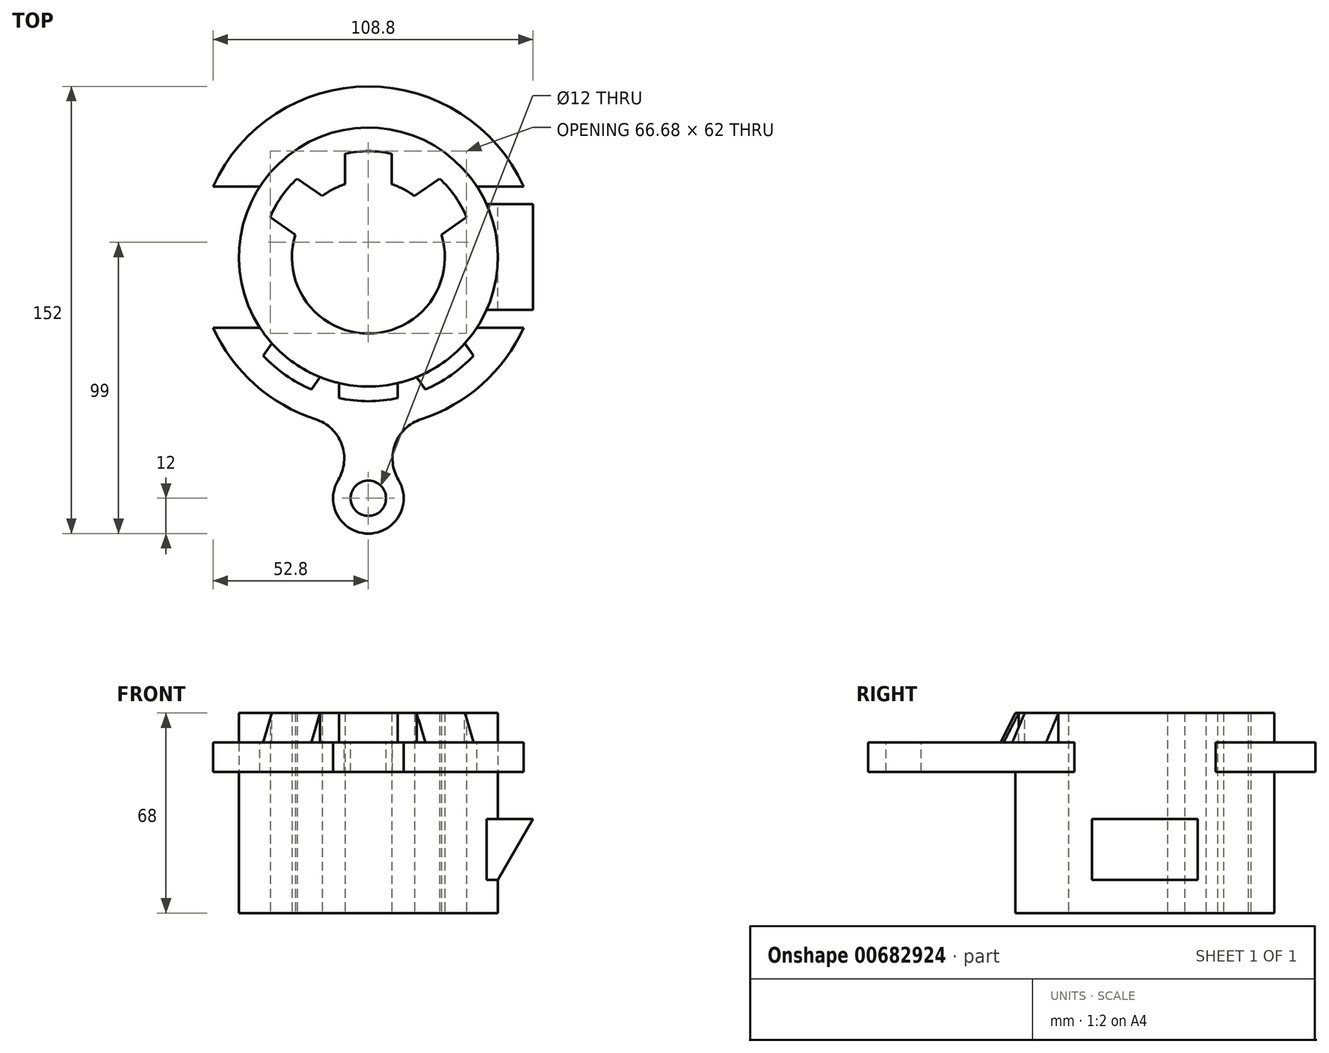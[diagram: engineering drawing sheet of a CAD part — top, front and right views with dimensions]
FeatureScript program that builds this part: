
annotation { "Feature Type Name" : "Feature", "Feature Type Description" : "" }
export const myFeature = defineFeature(function(context is Context, id is Id, definition is map)
    precondition{}
    {
        {
            var Q0;
            Q0=qCreatedBy(makeId("Top.planeOp"),FACE);
            var sketch = newSketch(context, id + "F0", { "sketchPlane" : qUnion([Q0])});
            skCircle(sketch, "E0", {"center": v(0, 0) * mm, "radius": 44 * mm});
            skArc(sketch, "E1", {"start": v(-8, 24.74) * mm, "mid": v(-12, -23.06) * mm, "end": v(24.85, 7.64) * mm});
            skLineSegment(sketch, "E2", {"start": v(-8, 24.74) * mm, "end": v(-8, 35.1) * mm});
            skLineSegment(sketch, "E3", {"start": v(8, 24.74) * mm, "end": v(8, 35.1) * mm});
            skArc(sketch, "E4", {"start": v(8, 35.1) * mm, "mid": v(0, 36) * mm, "end": v(-8, 35.1) * mm});
            skLineSegment(sketch, "E5", {"start": v(15.68, 20.74) * mm, "end": v(24.16, 26.69) * mm});
            skLineSegment(sketch, "E6", {"start": v(24.85, 7.64) * mm, "end": v(33.34, 13.58) * mm});
            skArc(sketch, "E7", {"start": v(33.34, 13.58) * mm, "mid": v(29.49, 20.65) * mm, "end": v(24.16, 26.69) * mm});
            skArc(sketch, "E8.trimOffspring", {"start": v(15.68, 20.74) * mm, "mid": v(12, 23.06) * mm, "end": v(8, 24.74) * mm});
            skLineSegment(sketch, "E9.1.0", {"start": v(-24.85, 7.64) * mm, "end": v(-33.34, 13.58) * mm});
            skArc(sketch, "E9.1.1", {"start": v(-24.16, 26.69) * mm, "mid": v(-29.49, 20.65) * mm, "end": v(-33.34, 13.58) * mm});
            skLineSegment(sketch, "E9.1.2", {"start": v(-15.68, 20.74) * mm, "end": v(-24.16, 26.69) * mm});
            skLineSegment(sketch, "E9.anchor1", {"start": v(0, 0) * mm, "end": v(15.68, 20.74) * mm, "construction": true});
            skLineSegment(sketch, "E9.anchor2", {"start": v(0, 0) * mm, "end": v(-24.85, 7.64) * mm, "construction": true});
            skSolve(sketch);
        }
        {
            var Q0;
            Q0=makeQuery(id+"F0.imprint","IMPRINT",FACE,{"disambiguationData":[TD([[makeQuery(id+"F0.imprint","IMPRINT",EDGE,{"derivedFrom":sQuery(id+"F0.wireOp",EDGE,"E0")}),1.0]])]});
            extrude(context, id + "F1", {"entities" : qUnion([Q0]), "endBound" : BoundingType.SYMMETRIC, "depth" : 68 * mm, "offsetDistance" : 25 * mm});
        }
        {
            var Q0;
            Q0=makeQuery(id+"F1.opExtrude","CAP_FACE",FACE,{"disambiguationData":[OSD([sQuery(id+"F0.wireOp",EDGE,"E0"),sQuery(id+"F0.wireOp",EDGE,"E1"),sQuery(id+"F0.wireOp",EDGE,"E2"),sQuery(id+"F0.wireOp",EDGE,"E3"),sQuery(id+"F0.wireOp",EDGE,"E4"),sQuery(id+"F0.wireOp",EDGE,"E5"),sQuery(id+"F0.wireOp",EDGE,"E6"),sQuery(id+"F0.wireOp",EDGE,"E7"),sQuery(id+"F0.wireOp",EDGE,"E8.trimOffspring"),sQuery(id+"F0.wireOp",EDGE,"E9.1.0"),sQuery(id+"F0.wireOp",EDGE,"E9.1.1"),sQuery(id+"F0.wireOp",EDGE,"E9.1.2")])],"isStart":false});
            cPlane(context, id + "F2", {"entities" : qUnion([Q0]), "cplaneType" : CPlaneType.OFFSET, "offset" : 10 * mm, "oppositeDirection" : true, "width" : 150 * mm, "height" : 150 * mm});
        }
        {
            var Q0;
            Q0=qCreatedBy(id+"F2.planeOp",FACE);
            var sketch = newSketch(context, id + "F3", { "sketchPlane" : qUnion([Q0])});
            skArc(sketch, "E10", {"start": v(-52.8, -24) * mm, "mid": v(-38.63, -43.26) * mm, "end": v(-17.9, -55.17) * mm});
            skLineSegment(sketch, "E11", {"start": v(-52.8, -24) * mm, "end": v(52.8, -24) * mm});
            skLineSegment(sketch, "E12", {"start": v(-52.8, 24) * mm, "end": v(52.8, 24) * mm});
            skArc(sketch, "E13.trimOffspring", {"start": v(52.8, 24) * mm, "mid": v(0, 58) * mm, "end": v(-52.8, 24) * mm});
            skCircle(sketch, "E14.0", {"center": v(0, 0) * mm, "radius": 44 * mm});
            skArc(sketch, "E15", {"start": v(-10.25, -75.76) * mm, "mid": v(0, -94) * mm, "end": v(10.25, -75.76) * mm});
            skCircle(sketch, "E16", {"center": v(0, -82) * mm, "radius": 6 * mm});
            skArc(sketch, "E17", {"start": v(-10.25, -75.76) * mm, "mid": v(-9.09, -63.62) * mm, "end": v(-17.9, -55.17) * mm});
            skArc(sketch, "E18", {"start": v(17.9, -55.17) * mm, "mid": v(9.09, -63.62) * mm, "end": v(10.25, -75.76) * mm});
            skArc(sketch, "E19.trimOffspring", {"start": v(17.9, -55.17) * mm, "mid": v(38.63, -43.26) * mm, "end": v(52.8, -24) * mm});
            skSolve(sketch);
        }
        {
            var Q0;
            {var subQ4=sQuery(id+"F3.wireOp",EDGE,"E10");Q0=makeQuery(id+"F3.imprint","IMPRINT",FACE,{"disambiguationData":[TD([[makeQuery(id+"F3.imprint","IMPRINT",EDGE,{"derivedFrom":subQ4}),1.0]])]});}
            var Q1;
            {var subQ0=sQuery(id+"F3.wireOp",EDGE,"E13.trimOffspring");Q1=makeQuery(id+"F3.imprint","IMPRINT",FACE,{"disambiguationData":[TD([[makeQuery(id+"F3.imprint","IMPRINT",EDGE,{"derivedFrom":subQ0}),1.0]])]});}
            extrude(context, id + "F4", {"entities" : qUnion([Q0, Q1]), "operationType" : NewBodyOperationType.ADD, "oppositeDirection" : true, "depth" : 10 * mm, "offsetDistance" : 25 * mm});
        }
        {
            var Q0;
            Q0=qCreatedBy(makeId("Front.planeOp"),FACE);
            var sketch = newSketch(context, id + "F5", { "sketchPlane" : qUnion([Q0])});
            skLineSegment(sketch, "E20", {"start": v(44, 34) * mm, "end": v(44, -34) * mm});
            skLineSegment(sketch, "E21", {"start": v(44, -2) * mm, "end": v(56, -2) * mm});
            skLineSegment(sketch, "E22", {"start": v(56, -2) * mm, "end": v(44, -22.78) * mm});
            skLineSegment(sketch, "E23", {"start": v(44, -22.78) * mm, "end": v(31.63, -22.78) * mm});
            skLineSegment(sketch, "E24", {"start": v(31.63, -22.78) * mm, "end": v(31.63, -2) * mm});
            skLineSegment(sketch, "E25", {"start": v(31.63, -2) * mm, "end": v(44, -2) * mm});
            skLineSegment(sketch, "E26.0", {"start": v(-44, -34) * mm, "end": v(44, -34) * mm});
            skSolve(sketch);
        }
        {
            var Q0;
            Q0 = qSketchRegion(id + "F5", true);
            extrude(context, id + "F6", {"entities" : qUnion([Q0]), "operationType" : NewBodyOperationType.ADD, "endBound" : BoundingType.SYMMETRIC, "depth" : 36 * mm, "offsetDistance" : 25 * mm});
        }
        {
            var Q0;
            Q0=makeQuery(id+"F1.opExtrude","CAP_FACE",FACE,{"disambiguationData":[OSD([sQuery(id+"F0.wireOp",EDGE,"E0"),sQuery(id+"F0.wireOp",EDGE,"E1"),sQuery(id+"F0.wireOp",EDGE,"E2"),sQuery(id+"F0.wireOp",EDGE,"E3"),sQuery(id+"F0.wireOp",EDGE,"E4"),sQuery(id+"F0.wireOp",EDGE,"E5"),sQuery(id+"F0.wireOp",EDGE,"E6"),sQuery(id+"F0.wireOp",EDGE,"E7"),sQuery(id+"F0.wireOp",EDGE,"E8.trimOffspring"),sQuery(id+"F0.wireOp",EDGE,"E9.1.0"),sQuery(id+"F0.wireOp",EDGE,"E9.1.1"),sQuery(id+"F0.wireOp",EDGE,"E9.1.2")])],"isStart":false});
            var sketch = newSketch(context, id + "F7", { "sketchPlane" : qUnion([Q0])});
            skCircle(sketch, "E27.0", {"center": v(0, 0) * mm, "radius": 44 * mm});
            skLineSegment(sketch, "E28", {"start": v(-10, -42.85) * mm, "end": v(-10, -47.97) * mm});
            skCircle(sketch, "E29", {"center": v(0, 0) * mm, "radius": 49 * mm});
            skLineSegment(sketch, "E30", {"start": v(10, -42.85) * mm, "end": v(10, -47.97) * mm});
            skLineSegment(sketch, "E31", {"start": v(0, 0) * mm, "end": v(0, -60.57) * mm, "construction": true});
            skLineSegment(sketch, "E32", {"start": v(16.39, -40.84) * mm, "end": v(32.77, -29.36) * mm});
            skLineSegment(sketch, "E33", {"start": v(0, 0) * mm, "end": v(25.24, -36.04) * mm});
            skLineSegment(sketch, "E34", {"start": v(16.39, -40.84) * mm, "end": v(19.32, -45.03) * mm});
            skLineSegment(sketch, "E35", {"start": v(32.77, -29.36) * mm, "end": v(35.7, -33.56) * mm});
            skLineSegment(sketch, "E36", {"start": v(-16.39, -40.84) * mm, "end": v(-19.32, -45.03) * mm});
            skLineSegment(sketch, "E37", {"start": v(-32.77, -29.36) * mm, "end": v(-35.7, -33.56) * mm});
            skLineSegment(sketch, "E38", {"start": v(-32.77, -29.36) * mm, "end": v(-16.39, -40.84) * mm});
            skLineSegment(sketch, "E39", {"start": v(0, 0) * mm, "end": v(-24.58, -35.1) * mm});
            skSolve(sketch);
        }
        {
            var Q0;
            {var subQ1=sQuery(id+"F7.wireOp",EDGE,"E36");Q0=makeQuery(id+"F7.imprint","IMPRINT",FACE,{"disambiguationData":[TD([[makeQuery(id+"F7.imprint","IMPRINT",EDGE,{"derivedFrom":subQ1}),-1.0]])]});}
            var Q1;
            {var subQ0=sQuery(id+"F7.wireOp",EDGE,"E28");Q1=makeQuery(id+"F7.imprint","IMPRINT",FACE,{"disambiguationData":[TD([[makeQuery(id+"F7.imprint","IMPRINT",EDGE,{"derivedFrom":subQ0}),1.0]])]});}
            var Q2;
            {var subQ0=sQuery(id+"F7.wireOp",EDGE,"E34");Q2=makeQuery(id+"F7.imprint","IMPRINT",FACE,{"disambiguationData":[TD([[makeQuery(id+"F7.imprint","IMPRINT",EDGE,{"derivedFrom":subQ0}),1.0]])]});}
            var Q3;
            Q3=makeQuery(id+"F4.opExtrude","CAP_FACE",FACE,{"disambiguationData":[OSD([sQuery(id+"F3.wireOp",EDGE,"E10"),sQuery(id+"F3.wireOp",EDGE,"E11"),sQuery(id+"F3.wireOp",EDGE,"E14.0"),sQuery(id+"F3.wireOp",EDGE,"E15"),sQuery(id+"F3.wireOp",EDGE,"E16"),sQuery(id+"F3.wireOp",EDGE,"E17"),sQuery(id+"F3.wireOp",EDGE,"E18"),sQuery(id+"F3.wireOp",EDGE,"E19.trimOffspring")])],"isStart":true});
            extrude(context, id + "F8", {"entities" : qUnion([Q0, Q1, Q2, Q3]), "operationType" : NewBodyOperationType.ADD, "endBound" : BoundingType.UP_TO_NEXT, "oppositeDirection" : true, "depth" : 25 * mm, "offsetDistance" : 25 * mm});
        }
        {
            var Q0;
            Q0=qCreatedBy(makeId("Right.planeOp"),FACE);
            var sketch = newSketch(context, id + "F9", { "sketchPlane" : qUnion([Q0])});
            skLineSegment(sketch, "E40", {"start": v(-44, -34) * mm, "end": v(-44, 14) * mm});
            skLineSegment(sketch, "E41.0", {"start": v(-29.36, 34) * mm, "end": v(44, 34) * mm});
            skLineSegment(sketch, "E42.0", {"start": v(-55.17, 24) * mm, "end": v(-75.76, 24) * mm});
            skLineSegment(sketch, "E43", {"start": v(-49, 24) * mm, "end": v(-49, 34) * mm});
            skLineSegment(sketch, "E44", {"start": v(-49, 24) * mm, "end": v(-44, 34) * mm});
            skLineSegment(sketch, "E45", {"start": v(-44, 34) * mm, "end": v(-49, 34) * mm});
            skLineSegment(sketch, "E46", {"start": v(0, 0) * mm, "end": v(0, 7.66) * mm});
            skSolve(sketch);
        }
        {
            var Q0;
            Q0 = qSketchRegion(id + "F9", true);
            var Q1;
            Q1=sQuery(id+"F9.wireOp",EDGE,"E46");
            revolve(context, id + "F10", {"operationType" : NewBodyOperationType.REMOVE, "entities" : qUnion([Q0]), "axis" : qUnion([Q1]), "revolveType" : RevolveType.FULL, "oppositeDirection" : true});
        }
        {
            var Q0;
            Q0=makeQuery(id+"F1.opExtrude","CAP_FACE",FACE,{"disambiguationData":[OSD([sQuery(id+"F0.wireOp",EDGE,"E0"),sQuery(id+"F0.wireOp",EDGE,"E1"),sQuery(id+"F0.wireOp",EDGE,"E2"),sQuery(id+"F0.wireOp",EDGE,"E3"),sQuery(id+"F0.wireOp",EDGE,"E4"),sQuery(id+"F0.wireOp",EDGE,"E5"),sQuery(id+"F0.wireOp",EDGE,"E6"),sQuery(id+"F0.wireOp",EDGE,"E7"),sQuery(id+"F0.wireOp",EDGE,"E8.trimOffspring"),sQuery(id+"F0.wireOp",EDGE,"E9.1.0"),sQuery(id+"F0.wireOp",EDGE,"E9.1.1"),sQuery(id+"F0.wireOp",EDGE,"E9.1.2")])],"isStart":true});
            var sketch = newSketch(context, id + "F11", { "sketchPlane" : qUnion([Q0])});
            skArc(sketch, "E47.0", {"start": v(-24.85, -7.64) * mm, "mid": v(0, 26) * mm, "end": v(24.85, -7.64) * mm});
            skLineSegment(sketch, "E48.0", {"start": v(-24.85, -7.64) * mm, "end": v(-33.34, -13.58) * mm});
            skArc(sketch, "E49.0", {"start": v(-24.16, -26.69) * mm, "mid": v(-29.49, -20.65) * mm, "end": v(-33.34, -13.58) * mm});
            skLineSegment(sketch, "E50.0", {"start": v(-15.68, -20.74) * mm, "end": v(-24.16, -26.69) * mm});
            skArc(sketch, "E51.0", {"start": v(-8, -24.74) * mm, "mid": v(-12, -23.06) * mm, "end": v(-15.68, -20.74) * mm});
            skPoint(sketch, "E52.0", {"position": v(-8, -29.92) * mm});
            skLineSegment(sketch, "E53.0", {"start": v(-8, -24.74) * mm, "end": v(-8, -35.1) * mm});
            skPoint(sketch, "E54.0", {"position": v(0, -36) * mm});
            skArc(sketch, "E55.0", {"start": v(8, -35.1) * mm, "mid": v(0, -36) * mm, "end": v(-8, -35.1) * mm});
            skLineSegment(sketch, "E56.0", {"start": v(8, -24.74) * mm, "end": v(8, -35.1) * mm});
            skPoint(sketch, "E57.0", {"position": v(12, -23.06) * mm});
            skArc(sketch, "E58.0", {"start": v(15.68, -20.74) * mm, "mid": v(12, -23.06) * mm, "end": v(8, -24.74) * mm});
            skLineSegment(sketch, "E59.0", {"start": v(15.68, -20.74) * mm, "end": v(24.16, -26.69) * mm});
            skArc(sketch, "E60.0", {"start": v(33.34, -13.58) * mm, "mid": v(29.49, -20.65) * mm, "end": v(24.16, -26.69) * mm});
            skPoint(sketch, "E61.0", {"position": v(29.1, -10.6) * mm});
            skLineSegment(sketch, "E62.0", {"start": v(24.85, -7.64) * mm, "end": v(33.34, -13.58) * mm});
            skSolve(sketch);
        }
        {
            var Q0;
            Q0=makeQuery(id+"F11.imprint","IMPRINT",FACE,{"disambiguationData":[TD([[makeQuery(id+"F11.imprint","IMPRINT",EDGE,{"derivedFrom":sQuery(id+"F11.wireOp",EDGE,"E47.0")}),-1.0]])]});
            extrude(context, id + "F12", {"entities" : qUnion([Q0]), "operationType" : NewBodyOperationType.REMOVE, "oppositeDirection" : true, "depth" : 107.2 * mm, "offsetDistance" : 25 * mm});
        }
    });
